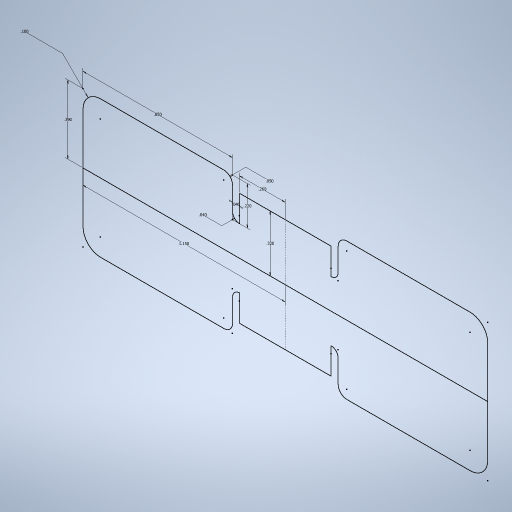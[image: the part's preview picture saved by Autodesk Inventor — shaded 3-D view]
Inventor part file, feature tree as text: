
AUTODESK INVENTOR PART (.ipt)
format: ipt  version: 2023 (Build 270158000, 158)  size: 255,488 bytes
history: native  units: in
note: dims shown in document units (in); Inventor stores cm internally (conversion verified against a paired STEP export)
features: sketch x1
ambient origin geometry x8: Origin, YZ Plane, XZ Plane, XY Plane, X Axis, Y Axis, Z Axis, Center Point
feature tree (1):
  sketch  "Sketch1"  dims[d0=1.15in d1=0.39in d2=0.85in d3=0.22in d4=0.04in d5=0.32in d6=0.26in d7=0.1in d8=0.05in d9=0.04in]
